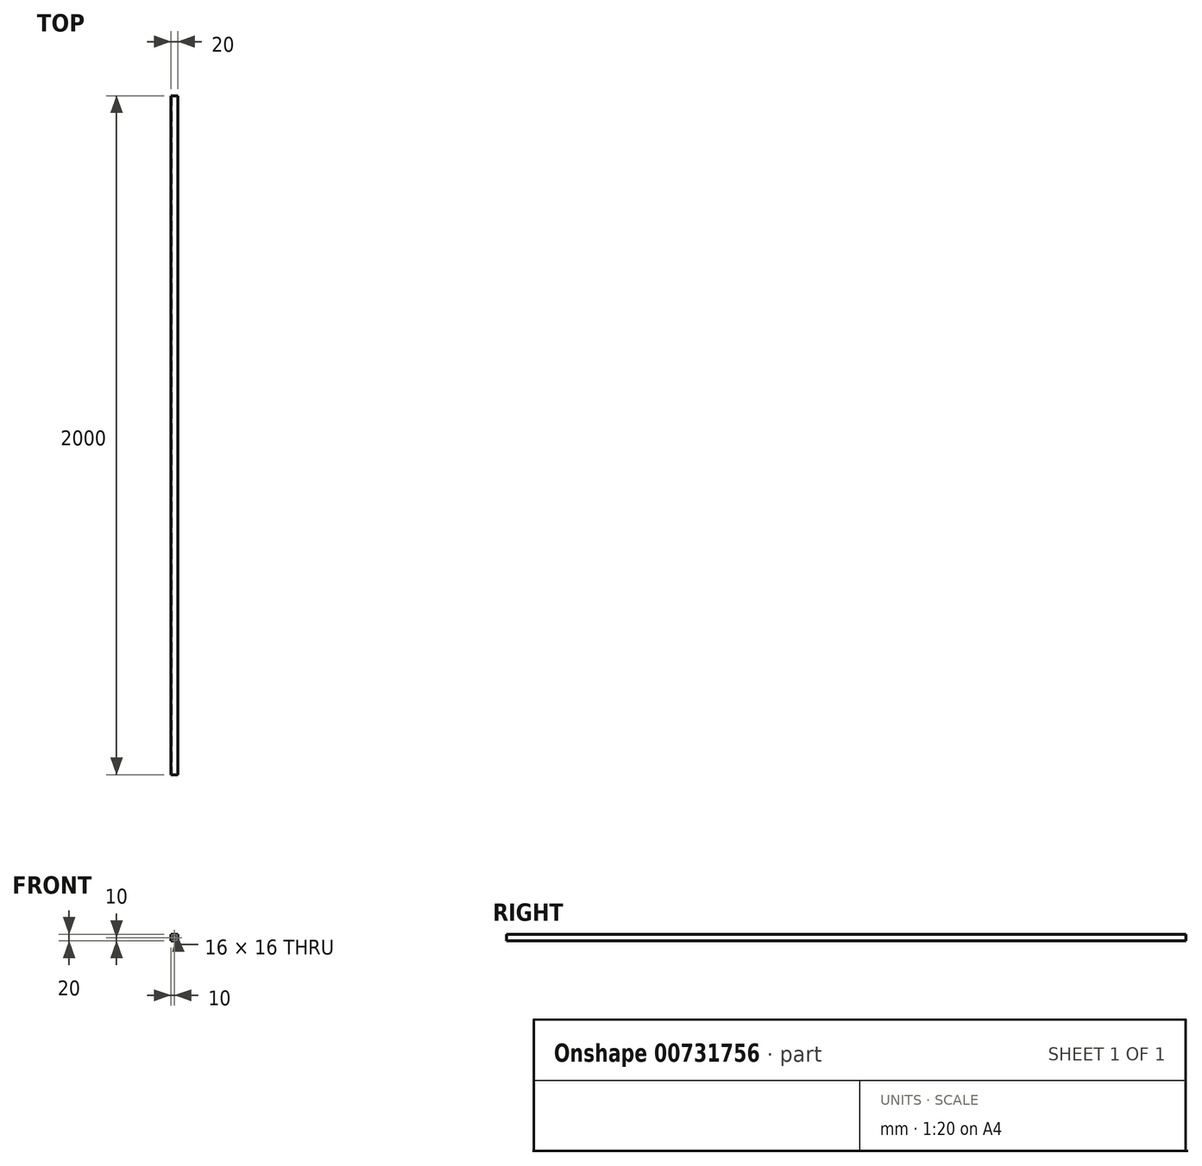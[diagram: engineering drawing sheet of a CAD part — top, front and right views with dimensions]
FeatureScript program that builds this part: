
annotation { "Feature Type Name" : "Feature", "Feature Type Description" : "" }
export const myFeature = defineFeature(function(context is Context, id is Id, definition is map)
    precondition{}
    {
        {
            var Q0;
            Q0=qCreatedBy(makeId("Front.planeOp"),FACE);
            var sketch = newSketch(context, id + "F0", { "sketchPlane" : qUnion([Q0])});
            skLineSegment(sketch, "E0.bottom", {"start": v(10, 10) * mm, "end": v(-10, 10) * mm});
            skLineSegment(sketch, "E0.top", {"start": v(10, -10) * mm, "end": v(-10, -10) * mm});
            skLineSegment(sketch, "E0.left", {"start": v(10, 10) * mm, "end": v(10, -10) * mm});
            skLineSegment(sketch, "E0.right", {"start": v(-10, 10) * mm, "end": v(-10, -10) * mm});
            skPoint(sketch, "E0.middle", {"position": v(0, 0) * mm});
            skLineSegment(sketch, "E1.0", {"start": v(8, 8) * mm, "end": v(-8, 8) * mm});
            skLineSegment(sketch, "E1.1", {"start": v(8, 8) * mm, "end": v(8, -8) * mm});
            skLineSegment(sketch, "E1.2", {"start": v(8, -8) * mm, "end": v(-8, -8) * mm});
            skLineSegment(sketch, "E1.3", {"start": v(-8, 8) * mm, "end": v(-8, -8) * mm});
            skSolve(sketch);
        }
        {
            var Q0;
            Q0=makeQuery(id+"F0.imprint","IMPRINT",FACE,{"disambiguationData":[TD([[makeQuery(id+"F0.imprint","IMPRINT",EDGE,{"derivedFrom":sQuery(id+"F0.wireOp",EDGE,"E0.bottom")}),1.0]])]});
            extrude(context, id + "F1", {"entities" : qUnion([Q0]), "oppositeDirection" : true, "depth" : 2000 * mm, "offsetDistance" : 25 * mm});
        }
    });
